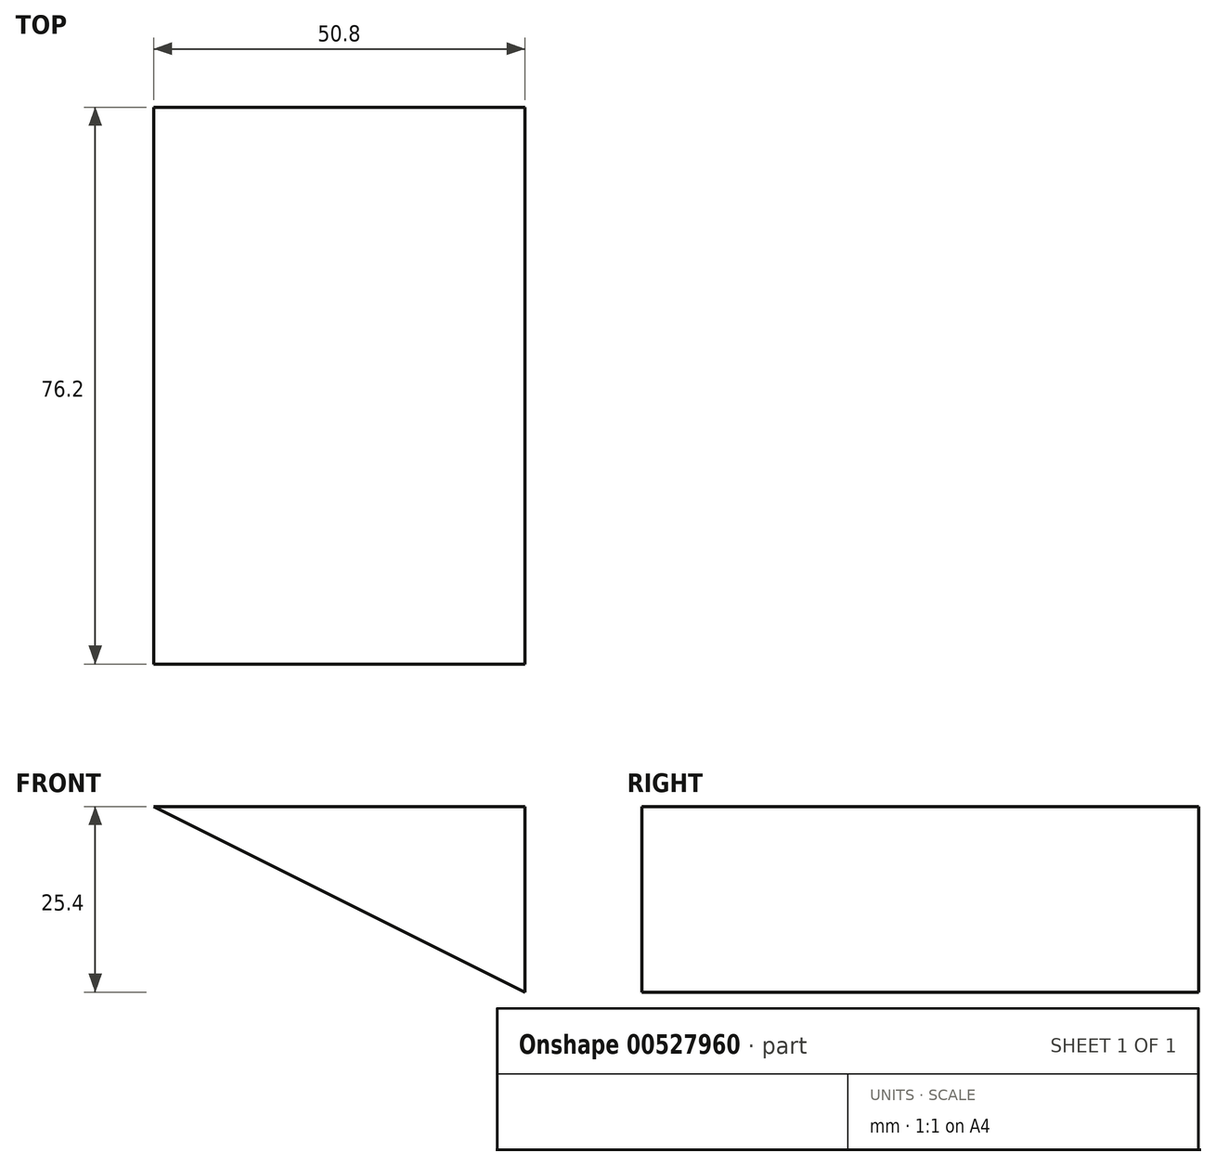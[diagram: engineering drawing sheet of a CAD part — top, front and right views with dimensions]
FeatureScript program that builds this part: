
annotation { "Feature Type Name" : "Feature", "Feature Type Description" : "" }
export const myFeature = defineFeature(function(context is Context, id is Id, definition is map)
    precondition{}
    {
        {
            var Q0;
            Q0=qCreatedBy(makeId("Front.planeOp"),FACE);
            var sketch = newSketch(context, id + "F0", { "sketchPlane" : qUnion([Q0])});
            skLineSegment(sketch, "E0", {"start": v(-29.63, 55.72) * mm, "end": v(21.17, 55.72) * mm});
            skLineSegment(sketch, "E1", {"start": v(21.17, 55.72) * mm, "end": v(21.17, 30.32) * mm});
            skLineSegment(sketch, "E2", {"start": v(21.17, 30.32) * mm, "end": v(-29.63, 30.32) * mm});
            skLineSegment(sketch, "E3", {"start": v(-29.63, 30.32) * mm, "end": v(-29.63, 55.72) * mm});
            skLineSegment(sketch, "E4", {"start": v(-29.63, 55.72) * mm, "end": v(21.17, 30.32) * mm});
            skSolve(sketch);
        }
        {
            var Q0;
            Q0=makeQuery(id+"F0.imprint","IMPRINT",FACE,{"disambiguationData":[TD([[makeQuery(id+"F0.imprint","IMPRINT",EDGE,{"derivedFrom":sQuery(id+"F0.wireOp",EDGE,"E0")}),-1.0]])]});
            extrude(context, id + "F1", {"entities" : qUnion([Q0]), "depth" : 76.2 * mm, "offsetDistance" : 25.4 * mm});
        }
    });
